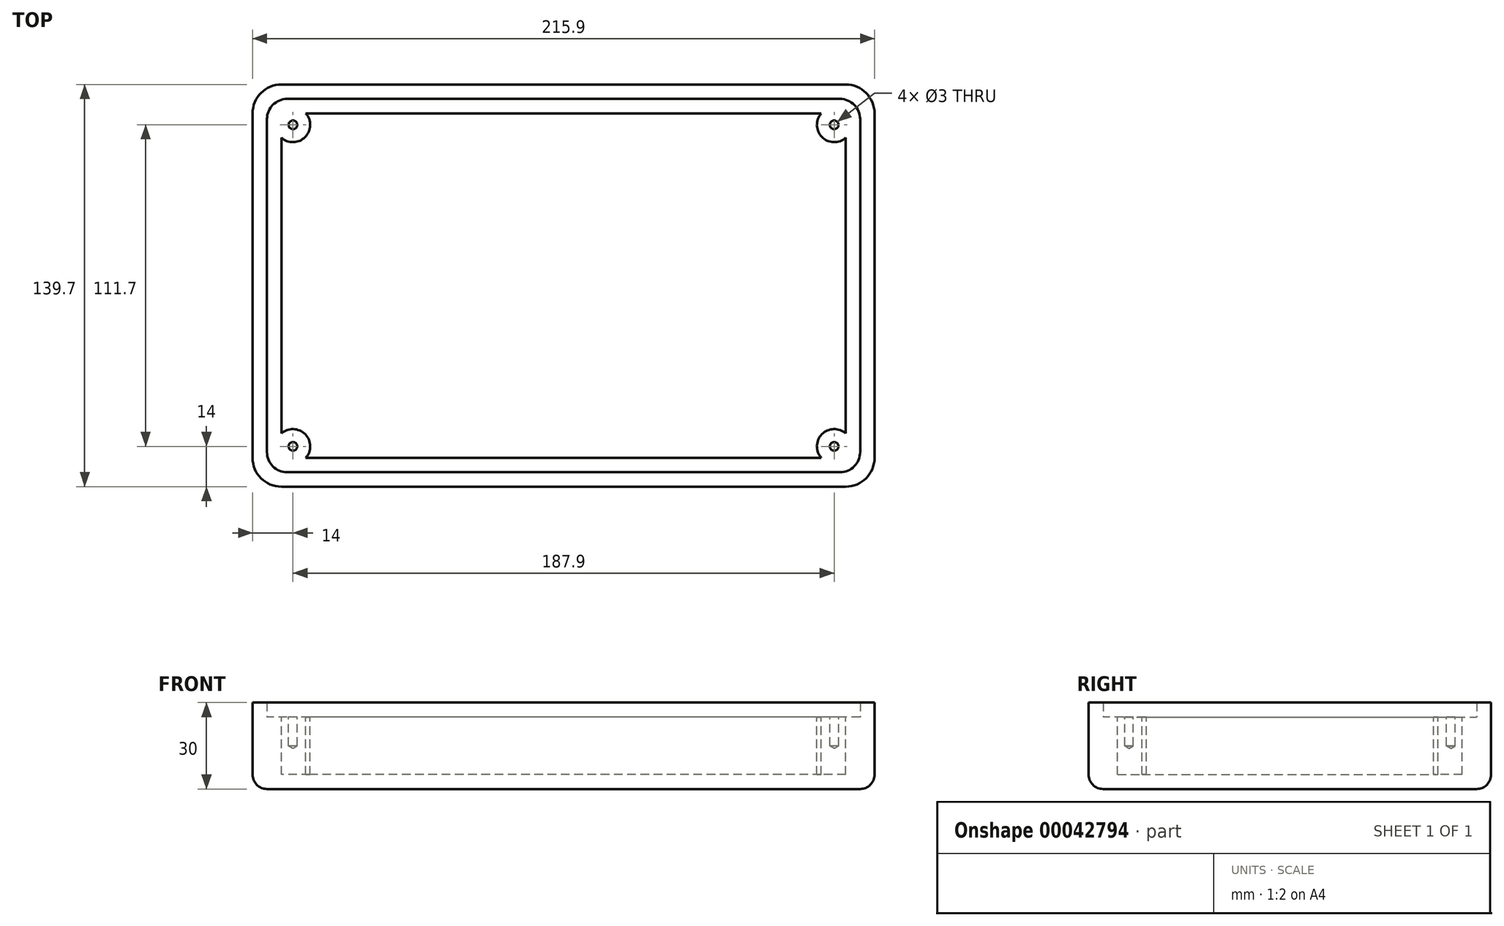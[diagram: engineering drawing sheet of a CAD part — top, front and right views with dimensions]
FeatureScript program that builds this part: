
annotation { "Feature Type Name" : "Feature", "Feature Type Description" : "" }
export const myFeature = defineFeature(function(context is Context, id is Id, definition is map)
    precondition{}
    {
        {
            var Q0;
            Q0=qCreatedBy(makeId("Top.planeOp"),FACE);
            var sketch = newSketch(context, id + "F0", { "sketchPlane" : qUnion([Q0])});
            skLineSegment(sketch, "E0.rect.bottom", {"start": v(97.95, -69.85) * mm, "end": v(-97.95, -69.85) * mm});
            skLineSegment(sketch, "E0.rect.top", {"start": v(97.95, 69.85) * mm, "end": v(-97.95, 69.85) * mm});
            skLineSegment(sketch, "E0.rect.left", {"start": v(107.95, -59.85) * mm, "end": v(107.95, 59.85) * mm});
            skLineSegment(sketch, "E0.rect.right", {"start": v(-107.95, -59.85) * mm, "end": v(-107.95, 59.85) * mm});
            skPoint(sketch, "E0.rect.middle", {"position": v(0, 0) * mm});
            skPoint(sketch, "E1.visualSharp", {"position": v(-107.95, 69.85) * mm});
            skArc(sketch, "E1.filletArc", {"start": v(-97.95, 69.85) * mm, "mid": v(-105.02, 66.92) * mm, "end": v(-107.95, 59.85) * mm});
            skPoint(sketch, "E2.visualSharp", {"position": v(107.95, 69.85) * mm});
            skArc(sketch, "E2.filletArc", {"start": v(107.95, 59.85) * mm, "mid": v(105.02, 66.92) * mm, "end": v(97.95, 69.85) * mm});
            skPoint(sketch, "E3.visualSharp", {"position": v(107.95, -69.85) * mm});
            skArc(sketch, "E3.filletArc", {"start": v(97.95, -69.85) * mm, "mid": v(105.02, -66.92) * mm, "end": v(107.95, -59.85) * mm});
            skPoint(sketch, "E4.visualSharp", {"position": v(-107.95, -69.85) * mm});
            skArc(sketch, "E4.filletArc", {"start": v(-107.95, -59.85) * mm, "mid": v(-105.02, -66.92) * mm, "end": v(-97.95, -69.85) * mm});
            skSolve(sketch);
        }
        {
            var Q0;
            Q0=makeQuery(id+"F0.imprint","IMPRINT",FACE,{"disambiguationData":[TD([[makeQuery(id+"F0.imprint","IMPRINT",EDGE,{"derivedFrom":sQuery(id+"F0.wireOp",EDGE,"E0.rect.bottom")}),-1.0]])]});
            extrude(context, id + "F1", {"entities" : qUnion([Q0]), "depth" : 30 * mm});
        }
        {
            var Q0;
            Q0=makeQuery(id+"F1.opExtrude","CAP_FACE",FACE,{"disambiguationData":[OSD([sQuery(id+"F0.wireOp",EDGE,"E0.rect.bottom"),sQuery(id+"F0.wireOp",EDGE,"E0.rect.top"),sQuery(id+"F0.wireOp",EDGE,"E0.rect.left"),sQuery(id+"F0.wireOp",EDGE,"E0.rect.right"),sQuery(id+"F0.wireOp",EDGE,"E1.filletArc"),sQuery(id+"F0.wireOp",EDGE,"E2.filletArc"),sQuery(id+"F0.wireOp",EDGE,"E3.filletArc"),sQuery(id+"F0.wireOp",EDGE,"E4.filletArc")])],"isStart":false});
            shell(context, id + "F2", {"entities" : qUnion([Q0]), "thickness" : 10 * mm});
        }
        {
            var Q0;
            Q0=makeQuery(id+"F2.opShell","OFFSET_FACE",FACE,{"disambiguationData":[OSD([sQuery(id+"F0.wireOp",EDGE,"E0.rect.bottom"),sQuery(id+"F0.wireOp",EDGE,"E0.rect.top"),sQuery(id+"F0.wireOp",EDGE,"E0.rect.left"),sQuery(id+"F0.wireOp",EDGE,"E0.rect.right"),sQuery(id+"F0.wireOp",EDGE,"E1.filletArc"),sQuery(id+"F0.wireOp",EDGE,"E2.filletArc"),sQuery(id+"F0.wireOp",EDGE,"E3.filletArc"),sQuery(id+"F0.wireOp",EDGE,"E4.filletArc")])]});
            cPlane(context, id + "F3", {"entities" : qUnion([Q0]), "cplaneType" : CPlaneType.OFFSET, "offset" : 15 * mm, "width" : 150 * mm, "height" : 150 * mm});
        }
        {
            var Q0;
            Q0=qCreatedBy(id+"F3.planeOp",FACE);
            var sketch = newSketch(context, id + "F4", { "sketchPlane" : qUnion([Q0])});
            skLineSegment(sketch, "E5.rect.bottom", {"start": v(95.95, -64.85) * mm, "end": v(-95.95, -64.85) * mm});
            skLineSegment(sketch, "E5.rect.top", {"start": v(95.95, 64.85) * mm, "end": v(-95.95, 64.85) * mm});
            skLineSegment(sketch, "E5.rect.left", {"start": v(102.95, -57.85) * mm, "end": v(102.95, 57.85) * mm});
            skLineSegment(sketch, "E5.rect.right", {"start": v(-102.95, -57.85) * mm, "end": v(-102.95, 57.85) * mm});
            skPoint(sketch, "E5.rect.middle", {"position": v(0, 0) * mm});
            skPoint(sketch, "E6.visualSharp", {"position": v(-102.95, 64.85) * mm});
            skArc(sketch, "E6.filletArc", {"start": v(-95.95, 64.85) * mm, "mid": v(-100.9, 62.8) * mm, "end": v(-102.95, 57.85) * mm});
            skPoint(sketch, "E7.visualSharp", {"position": v(102.95, 64.85) * mm});
            skArc(sketch, "E7.filletArc", {"start": v(102.95, 57.85) * mm, "mid": v(100.9, 62.8) * mm, "end": v(95.95, 64.85) * mm});
            skPoint(sketch, "E8.visualSharp", {"position": v(102.95, -64.85) * mm});
            skArc(sketch, "E8.filletArc", {"start": v(95.95, -64.85) * mm, "mid": v(100.9, -62.8) * mm, "end": v(102.95, -57.85) * mm});
            skPoint(sketch, "E9.visualSharp", {"position": v(-102.95, -64.85) * mm});
            skArc(sketch, "E9.filletArc", {"start": v(-102.95, -57.85) * mm, "mid": v(-100.9, -62.8) * mm, "end": v(-95.95, -64.85) * mm});
            skSolve(sketch);
        }
        {
            var Q0;
            Q0=makeQuery(id+"F4.imprint","IMPRINT",FACE,{"disambiguationData":[TD([[makeQuery(id+"F4.imprint","IMPRINT",EDGE,{"derivedFrom":sQuery(id+"F4.wireOp",EDGE,"E5.rect.bottom")}),-1.0]])]});
            extrude(context, id + "F5", {"entities" : qUnion([Q0]), "operationType" : NewBodyOperationType.REMOVE, "depth" : 25 * mm});
        }
        {
            var Q0;
            Q0=makeQuery(id+"F5.boolean.opBoolean","COPY",FACE,{"derivedFrom":makeQuery(id+"F5.opExtrude","CAP_FACE",FACE,{"disambiguationData":[OSD([sQuery(id+"F4.wireOp",EDGE,"E5.rect.bottom"),sQuery(id+"F4.wireOp",EDGE,"E5.rect.top"),sQuery(id+"F4.wireOp",EDGE,"E5.rect.left"),sQuery(id+"F4.wireOp",EDGE,"E5.rect.right"),sQuery(id+"F4.wireOp",EDGE,"E6.filletArc"),sQuery(id+"F4.wireOp",EDGE,"E7.filletArc"),sQuery(id+"F4.wireOp",EDGE,"E8.filletArc"),sQuery(id+"F4.wireOp",EDGE,"E9.filletArc")])],"isStart":true})});
            var sketch = newSketch(context, id + "F6", { "sketchPlane" : qUnion([Q0])});
            skLineSegment(sketch, "E10.rect.bottom", {"start": v(-93.95, 55.85) * mm, "end": v(93.95, 55.85) * mm});
            skLineSegment(sketch, "E10.rect.top", {"start": v(-93.95, -55.85) * mm, "end": v(93.95, -55.85) * mm});
            skLineSegment(sketch, "E10.rect.left", {"start": v(-93.95, 55.85) * mm, "end": v(-93.95, -55.85) * mm});
            skLineSegment(sketch, "E10.rect.right", {"start": v(93.95, 55.85) * mm, "end": v(93.95, -55.85) * mm});
            skPoint(sketch, "E10.rect.middle", {"position": v(0, 0) * mm});
            skCircle(sketch, "E11", {"center": v(-93.95, 55.85) * mm, "radius": 6 * mm});
            skCircle(sketch, "E12.MirrorC", {"center": v(93.95, 55.85) * mm, "radius": 6 * mm});
            skCircle(sketch, "E13.MirrorC", {"center": v(93.95, -55.85) * mm, "radius": 6 * mm});
            skCircle(sketch, "E14.MirrorC", {"center": v(-93.95, -55.85) * mm, "radius": 6 * mm});
            skSolve(sketch);
        }
        {
            var Q0;
            Q0=makeQuery(id+"F2.opShell","OFFSET_FACE",FACE,{"disambiguationData":[OSD([sQuery(id+"F0.wireOp",EDGE,"E0.rect.bottom"),sQuery(id+"F0.wireOp",EDGE,"E0.rect.top"),sQuery(id+"F0.wireOp",EDGE,"E0.rect.left"),sQuery(id+"F0.wireOp",EDGE,"E0.rect.right"),sQuery(id+"F0.wireOp",EDGE,"E1.filletArc"),sQuery(id+"F0.wireOp",EDGE,"E2.filletArc"),sQuery(id+"F0.wireOp",EDGE,"E3.filletArc"),sQuery(id+"F0.wireOp",EDGE,"E4.filletArc")])]});
            var sketch = newSketch(context, id + "F7", { "sketchPlane" : qUnion([Q0])});
            skSolve(sketch);
        }
        {
            var Q0;
            {var subQ3=sQuery(id+"F0.wireOp",EDGE,"E0.rect.bottom");Q0=makeQuery(id+"F7.imprint","IMPRINT",FACE,{"disambiguationData":[TD([[makeQuery(id+"F7.imprint","IMPRINT",EDGE,{"derivedFrom":makeQuery(id+"F2.opShell","OFFSET_EDGE",EDGE,{"disambiguationData":[OSD([subQ3]),TDD([makeQuery(id+"F1.opExtrude","CAP_EDGE",EDGE,{"disambiguationData":[OSD([subQ3])],"isStart":true})])]})}),-1.0]])]});}
            extrude(context, id + "F8", {"entities" : qUnion([Q0]), "operationType" : NewBodyOperationType.REMOVE, "oppositeDirection" : true, "depth" : 5 * mm});
        }
        {
            var Q0;
            {var subQ7=sQuery(id+"F6.wireOp",EDGE,"E10.rect.bottom");var subQ9=sQuery(id+"F6.wireOp",EDGE,"E10.rect.left");var subQ10=makeQuery(id+"F6.imprint","INTERSECT",VERTEX,{"derivedFrom":[subQ7,subQ9]});Q0=makeQuery(id+"F6.imprint","IMPRINT",FACE,{"disambiguationData":[TD([[makeQuery(id+"F6.imprint","IMPRINT",EDGE,{"disambiguationData":[TD([[subQ10,-1.0]])],"derivedFrom":subQ7}),1.0]])]});}
            var Q1;
            {var subQ1=sQuery(id+"F6.wireOp",EDGE,"E10.rect.left");var subQ3=sQuery(id+"F6.wireOp",EDGE,"E10.rect.bottom");var subQ5=makeQuery(id+"F6.imprint","INTERSECT",VERTEX,{"derivedFrom":[subQ3,subQ1]});Q1=makeQuery(id+"F6.imprint","IMPRINT",FACE,{"disambiguationData":[TD([[makeQuery(id+"F6.imprint","IMPRINT",EDGE,{"disambiguationData":[TD([[subQ5,-1.0]])],"derivedFrom":subQ3}),-1.0]])]});}
            var Q2;
            {var subQ1=sQuery(id+"F6.wireOp",EDGE,"E10.rect.right");var subQ3=sQuery(id+"F6.wireOp",EDGE,"E10.rect.bottom");var subQ5=makeQuery(id+"F6.imprint","INTERSECT",VERTEX,{"derivedFrom":[subQ3,subQ1]});Q2=makeQuery(id+"F6.imprint","IMPRINT",FACE,{"disambiguationData":[TD([[makeQuery(id+"F6.imprint","IMPRINT",EDGE,{"disambiguationData":[TD([[subQ5,1.0]])],"derivedFrom":subQ3}),-1.0]])]});}
            var Q3;
            {var subQ7=sQuery(id+"F6.wireOp",EDGE,"E10.rect.bottom");var subQ9=sQuery(id+"F6.wireOp",EDGE,"E10.rect.right");var subQ10=makeQuery(id+"F6.imprint","INTERSECT",VERTEX,{"derivedFrom":[subQ7,subQ9]});Q3=makeQuery(id+"F6.imprint","IMPRINT",FACE,{"disambiguationData":[TD([[makeQuery(id+"F6.imprint","IMPRINT",EDGE,{"disambiguationData":[TD([[subQ10,1.0]])],"derivedFrom":subQ7}),1.0]])]});}
            var Q4;
            {var subQ1=sQuery(id+"F6.wireOp",EDGE,"E10.rect.right");var subQ3=sQuery(id+"F6.wireOp",EDGE,"E10.rect.top");var subQ5=makeQuery(id+"F6.imprint","INTERSECT",VERTEX,{"derivedFrom":[subQ3,subQ1]});Q4=makeQuery(id+"F6.imprint","IMPRINT",FACE,{"disambiguationData":[TD([[makeQuery(id+"F6.imprint","IMPRINT",EDGE,{"disambiguationData":[TD([[subQ5,1.0]])],"derivedFrom":subQ3}),1.0]])]});}
            var Q5;
            {var subQ6=sQuery(id+"F6.wireOp",EDGE,"E10.rect.top");var subQ8=sQuery(id+"F6.wireOp",EDGE,"E10.rect.right");var subQ9=makeQuery(id+"F6.imprint","INTERSECT",VERTEX,{"derivedFrom":[subQ6,subQ8]});Q5=makeQuery(id+"F6.imprint","IMPRINT",FACE,{"disambiguationData":[TD([[makeQuery(id+"F6.imprint","IMPRINT",EDGE,{"disambiguationData":[TD([[subQ9,1.0]])],"derivedFrom":subQ6}),-1.0]])]});}
            var Q6;
            {var subQ7=sQuery(id+"F6.wireOp",EDGE,"E10.rect.left");var subQ9=sQuery(id+"F6.wireOp",EDGE,"E10.rect.top");var subQ10=makeQuery(id+"F6.imprint","INTERSECT",VERTEX,{"derivedFrom":[subQ9,subQ7]});Q6=makeQuery(id+"F6.imprint","IMPRINT",FACE,{"disambiguationData":[TD([[makeQuery(id+"F6.imprint","IMPRINT",EDGE,{"disambiguationData":[TD([[subQ10,-1.0]])],"derivedFrom":subQ9}),-1.0]])]});}
            var Q7;
            {var subQ1=sQuery(id+"F6.wireOp",EDGE,"E10.rect.left");var subQ3=sQuery(id+"F6.wireOp",EDGE,"E10.rect.top");var subQ5=makeQuery(id+"F6.imprint","INTERSECT",VERTEX,{"derivedFrom":[subQ3,subQ1]});Q7=makeQuery(id+"F6.imprint","IMPRINT",FACE,{"disambiguationData":[TD([[makeQuery(id+"F6.imprint","IMPRINT",EDGE,{"disambiguationData":[TD([[subQ5,-1.0]])],"derivedFrom":subQ3}),1.0]])]});}
            extrude(context, id + "F9", {"entities" : qUnion([Q0, Q1, Q2, Q3, Q4, Q5, Q6, Q7]), "operationType" : NewBodyOperationType.ADD, "endBound" : BoundingType.UP_TO_NEXT, "oppositeDirection" : true, "depth" : 25 * mm});
        }
        {
            var Q0;
            Q0=sQuery(id+"F6.wireOp",VERTEX,"E11.center");
            var Q1;
            Q1=sQuery(id+"F6.wireOp",VERTEX,"E14.MirrorC.center");
            var Q2;
            Q2=sQuery(id+"F6.wireOp",VERTEX,"E13.MirrorC.center");
            var Q3;
            Q3=sQuery(id+"F6.wireOp",VERTEX,"E12.MirrorC.center");
            var Q4;
            Q4=makeQuery(id+"F1.opExtrude","SWEPT_BODY",BODY,{"disambiguationData":[OSD([sQuery(id+"F0.wireOp",EDGE,"E0.rect.bottom"),sQuery(id+"F0.wireOp",EDGE,"E0.rect.top"),sQuery(id+"F0.wireOp",EDGE,"E0.rect.left"),sQuery(id+"F0.wireOp",EDGE,"E0.rect.right"),sQuery(id+"F0.wireOp",EDGE,"E1.filletArc"),sQuery(id+"F0.wireOp",EDGE,"E2.filletArc"),sQuery(id+"F0.wireOp",EDGE,"E3.filletArc"),sQuery(id+"F0.wireOp",EDGE,"E4.filletArc")])]});
            hole(context, id + "F10", {"style" : HoleStyle.SIMPLE, "holeDiameter" : 3 * mm, "endStyle" : HoleEndStyle.BLIND, "holeDepth" : 10 * mm, "locations" : qUnion([Q0, Q1, Q2, Q3]), "scope" : qUnion([Q4])});
        }
        {
            var Q0;
            Q0=makeQuery(id+"F1.opExtrude","CAP_EDGE",EDGE,{"disambiguationData":[OSD([sQuery(id+"F0.wireOp",EDGE,"E0.rect.right")])],"isStart":true});
            fillet(context, id + "F11", {"entities" : qUnion([Q0]), "radius" : 5 * mm, "tangentPropagation" : true, "allowEdgeOverflow" : false});
        }
    });
